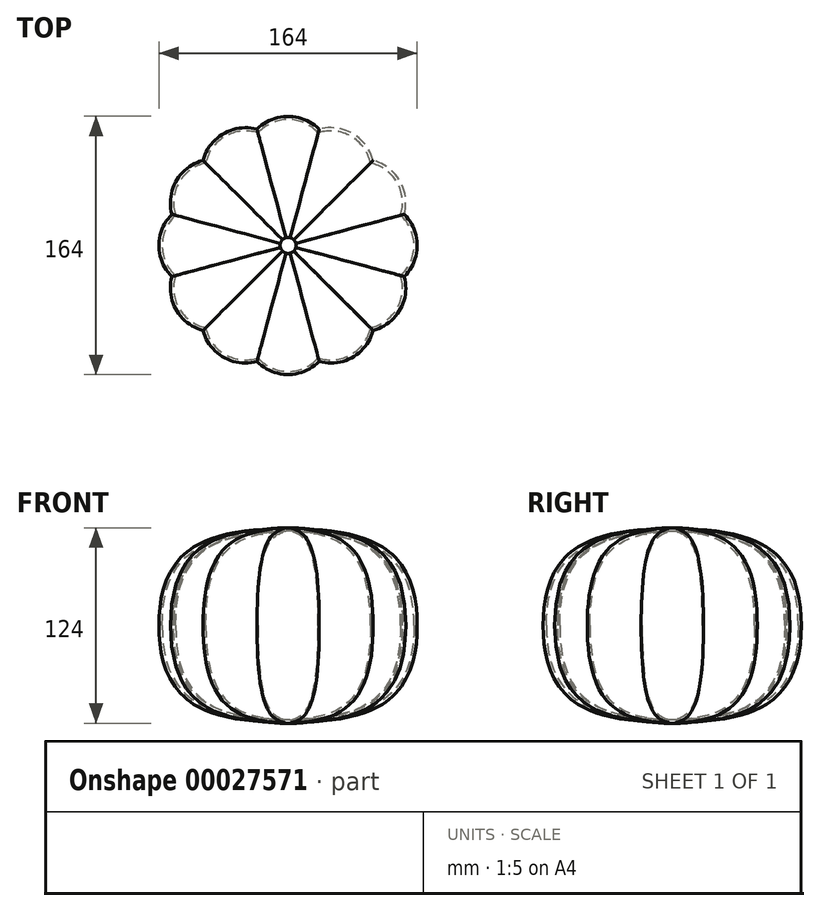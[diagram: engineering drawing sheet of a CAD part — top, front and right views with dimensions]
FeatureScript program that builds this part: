
annotation { "Feature Type Name" : "Feature", "Feature Type Description" : "" }
export const myFeature = defineFeature(function(context is Context, id is Id, definition is map)
    precondition{}
    {
        {
            var Q0;
            Q0=qCreatedBy(makeId("Top.planeOp"),FACE);
            var sketch = newSketch(context, id + "F0", { "sketchPlane" : qUnion([Q0])});
            skCircle(sketch, "E0", {"center": v(0, 0) * mm, "radius": 80 * mm, "construction": true});
            skLineSegment(sketch, "E1", {"start": v(0, 0) * mm, "end": v(20.7, 77.27) * mm});
            skLineSegment(sketch, "E2.MirrorCS", {"start": v(0, 0) * mm, "end": v(-20.7, 77.27) * mm});
            skArc(sketch, "E3", {"start": v(19.15, 71.48) * mm, "mid": v(0, 80) * mm, "end": v(-19.15, 71.48) * mm});
            skSolve(sketch);
        }
        {
            var Q0;
            Q0=qCreatedBy(makeId("Top.planeOp"),FACE);
            cPlane(context, id + "F1", {"entities" : qUnion([Q0]), "cplaneType" : CPlaneType.OFFSET, "offset" : 60 * mm, "width" : 150 * mm, "height" : 150 * mm});
        }
        {
            var Q0;
            Q0=qCreatedBy(id+"F1.planeOp",FACE);
            var sketch = newSketch(context, id + "F2", { "sketchPlane" : qUnion([Q0])});
            skLineSegment(sketch, "E4.0", {"start": v(0, 0) * mm, "end": v(-20.7, 77.27) * mm});
            skLineSegment(sketch, "E4.1", {"start": v(0, 0) * mm, "end": v(20.7, 77.27) * mm});
            skArc(sketch, "E5", {"start": v(1.3, 4.83) * mm, "mid": v(0, 5) * mm, "end": v(-1.3, 4.83) * mm});
            skSolve(sketch);
        }
        {
            var Q0;
            {var subQ3=sQuery(id+"F0.wireOp",EDGE,"E3");Q0=makeQuery(id+"F0.imprint","IMPRINT",FACE,{"disambiguationData":[TD([[makeQuery(id+"F0.imprint","IMPRINT",EDGE,{"derivedFrom":subQ3}),1.0]])]});}
            var Q1;
            Q1 = qSketchRegion(id + "F2", true);
            loft(context, id + "F3", {"startCondition" : LoftEndDerivativeType.NORMAL_TO_PROFILE, "startMagnitude" : 2.6, "endCondition" : LoftEndDerivativeType.NORMAL_TO_PROFILE, "endMagnitude" : 0, "sheetProfilesArray" : [{ "sheetProfileEntities" : qUnion([Q0]) }, { "sheetProfileEntities" : qUnion([Q1]) }]});
        }
        {
            var Q0;
            Q0=qCreatedBy(makeId("Front.planeOp"),FACE);
            var sketch = newSketch(context, id + "F4", { "sketchPlane" : qUnion([Q0])});
            skLineSegment(sketch, "E6", {"start": v(0, 0) * mm, "end": v(0, 72.55) * mm});
            skSolve(sketch);
        }
        {
            var Q0;
            {var subQ3=sQuery(id+"F2.wireOp",EDGE,"E5");var subQ7=sQuery(id+"F0.wireOp",EDGE,"E3");Q0=makeQuery(id+"F3.opLoft","SWEPT_BODY",BODY,{"disambiguationData":[OSD([makeQuery(id+"F0.imprint","IMPRINT",FACE,{"disambiguationData":[TD([[makeQuery(id+"F0.imprint","IMPRINT",EDGE,{"derivedFrom":subQ7}),1.0]])]}),makeQuery(id+"F2.imprint","IMPRINT",FACE,{"disambiguationData":[TD([[makeQuery(id+"F2.imprint","IMPRINT",EDGE,{"derivedFrom":subQ3}),1.0]])]})])]});}
            var Q1;
            Q1=sQuery(id+"F4.wireOp",EDGE,"E6");
            circularPattern(context, id + "F5", {"operationType" : NewBodyOperationType.ADD, "entities" : qUnion([Q0]), "axis" : qUnion([Q1]), "angle" : 360 * degree, "instanceCount" : 12, "equalSpace" : true});
        }
        {
            var Q0;
            {var subQ3=sQuery(id+"F2.wireOp",EDGE,"E5");var subQ7=sQuery(id+"F0.wireOp",EDGE,"E3");Q0=makeQuery(id+"F3.opLoft","SWEPT_BODY",BODY,{"disambiguationData":[OSD([makeQuery(id+"F0.imprint","IMPRINT",FACE,{"disambiguationData":[TD([[makeQuery(id+"F0.imprint","IMPRINT",EDGE,{"derivedFrom":subQ7}),1.0]])]}),makeQuery(id+"F2.imprint","IMPRINT",FACE,{"disambiguationData":[TD([[makeQuery(id+"F2.imprint","IMPRINT",EDGE,{"derivedFrom":subQ3}),1.0]])]})])]});}
            var Q1;
            {var subQ3=sQuery(id+"F0.wireOp",EDGE,"E3");var subQ4=makeQuery(id+"F3.opLoft","CAP_FACE",FACE,{"disambiguationData":[OSD([makeQuery(id+"F0.imprint","IMPRINT",FACE,{"disambiguationData":[TD([[makeQuery(id+"F0.imprint","IMPRINT",EDGE,{"derivedFrom":subQ3}),1.0]])]})])],"isStart":true});Q1=makeQuery(id+"F5.boolean.opBoolean","MERGE",FACE,{"derivedFrom":[subQ4,makeQuery(id+"F5.opPattern","COPY",FACE,{"derivedFrom":subQ4,"instanceName":"1"}),makeQuery(id+"F5.opPattern","COPY",FACE,{"derivedFrom":subQ4,"instanceName":"2"}),makeQuery(id+"F5.opPattern","COPY",FACE,{"derivedFrom":subQ4,"instanceName":"3"}),makeQuery(id+"F5.opPattern","COPY",FACE,{"derivedFrom":subQ4,"instanceName":"4"}),makeQuery(id+"F5.opPattern","COPY",FACE,{"derivedFrom":subQ4,"instanceName":"5"}),makeQuery(id+"F5.opPattern","COPY",FACE,{"derivedFrom":subQ4,"instanceName":"6"}),makeQuery(id+"F5.opPattern","COPY",FACE,{"derivedFrom":subQ4,"instanceName":"7"}),makeQuery(id+"F5.opPattern","COPY",FACE,{"derivedFrom":subQ4,"instanceName":"8"}),makeQuery(id+"F5.opPattern","COPY",FACE,{"derivedFrom":subQ4,"instanceName":"9"}),makeQuery(id+"F5.opPattern","COPY",FACE,{"derivedFrom":subQ4,"instanceName":"10"}),makeQuery(id+"F5.opPattern","COPY",FACE,{"derivedFrom":subQ4,"instanceName":"11"})]});}
            mirror(context, id + "F6", {"operationType" : NewBodyOperationType.ADD, "entities" : qUnion([Q0]), "mirrorPlane" : qUnion([Q1])});
        }
        {
            var Q0;
            {var subQ3=sQuery(id+"F2.wireOp",EDGE,"E5");var subQ4=makeQuery(id+"F3.opLoft","CAP_FACE",FACE,{"disambiguationData":[OSD([makeQuery(id+"F2.imprint","IMPRINT",FACE,{"disambiguationData":[TD([[makeQuery(id+"F2.imprint","IMPRINT",EDGE,{"derivedFrom":subQ3}),1.0]])]})])],"isStart":true});Q0=makeQuery(id+"F5.boolean.opBoolean","MERGE",FACE,{"derivedFrom":[subQ4,makeQuery(id+"F5.opPattern","COPY",FACE,{"derivedFrom":subQ4,"instanceName":"1"}),makeQuery(id+"F5.opPattern","COPY",FACE,{"derivedFrom":subQ4,"instanceName":"2"}),makeQuery(id+"F5.opPattern","COPY",FACE,{"derivedFrom":subQ4,"instanceName":"3"}),makeQuery(id+"F5.opPattern","COPY",FACE,{"derivedFrom":subQ4,"instanceName":"4"}),makeQuery(id+"F5.opPattern","COPY",FACE,{"derivedFrom":subQ4,"instanceName":"5"}),makeQuery(id+"F5.opPattern","COPY",FACE,{"derivedFrom":subQ4,"instanceName":"6"}),makeQuery(id+"F5.opPattern","COPY",FACE,{"derivedFrom":subQ4,"instanceName":"7"}),makeQuery(id+"F5.opPattern","COPY",FACE,{"derivedFrom":subQ4,"instanceName":"8"}),makeQuery(id+"F5.opPattern","COPY",FACE,{"derivedFrom":subQ4,"instanceName":"9"}),makeQuery(id+"F5.opPattern","COPY",FACE,{"derivedFrom":subQ4,"instanceName":"10"}),makeQuery(id+"F5.opPattern","COPY",FACE,{"derivedFrom":subQ4,"instanceName":"11"})]});}
            var Q1;
            {var subQ3=sQuery(id+"F2.wireOp",EDGE,"E5");var subQ7=sQuery(id+"F0.wireOp",EDGE,"E3");Q1=makeQuery(id+"F3.opLoft","SWEPT_BODY",BODY,{"disambiguationData":[OSD([makeQuery(id+"F0.imprint","IMPRINT",FACE,{"disambiguationData":[TD([[makeQuery(id+"F0.imprint","IMPRINT",EDGE,{"derivedFrom":subQ7}),1.0]])]}),makeQuery(id+"F2.imprint","IMPRINT",FACE,{"disambiguationData":[TD([[makeQuery(id+"F2.imprint","IMPRINT",EDGE,{"derivedFrom":subQ3}),1.0]])]})])]});}
            shell(context, id + "F7", {"isHollow" : true, "entities" : qUnion([Q0]), "parts" : qUnion([Q1]), "thickness" : 2 * mm, "oppositeDirection" : true});
        }
    });
